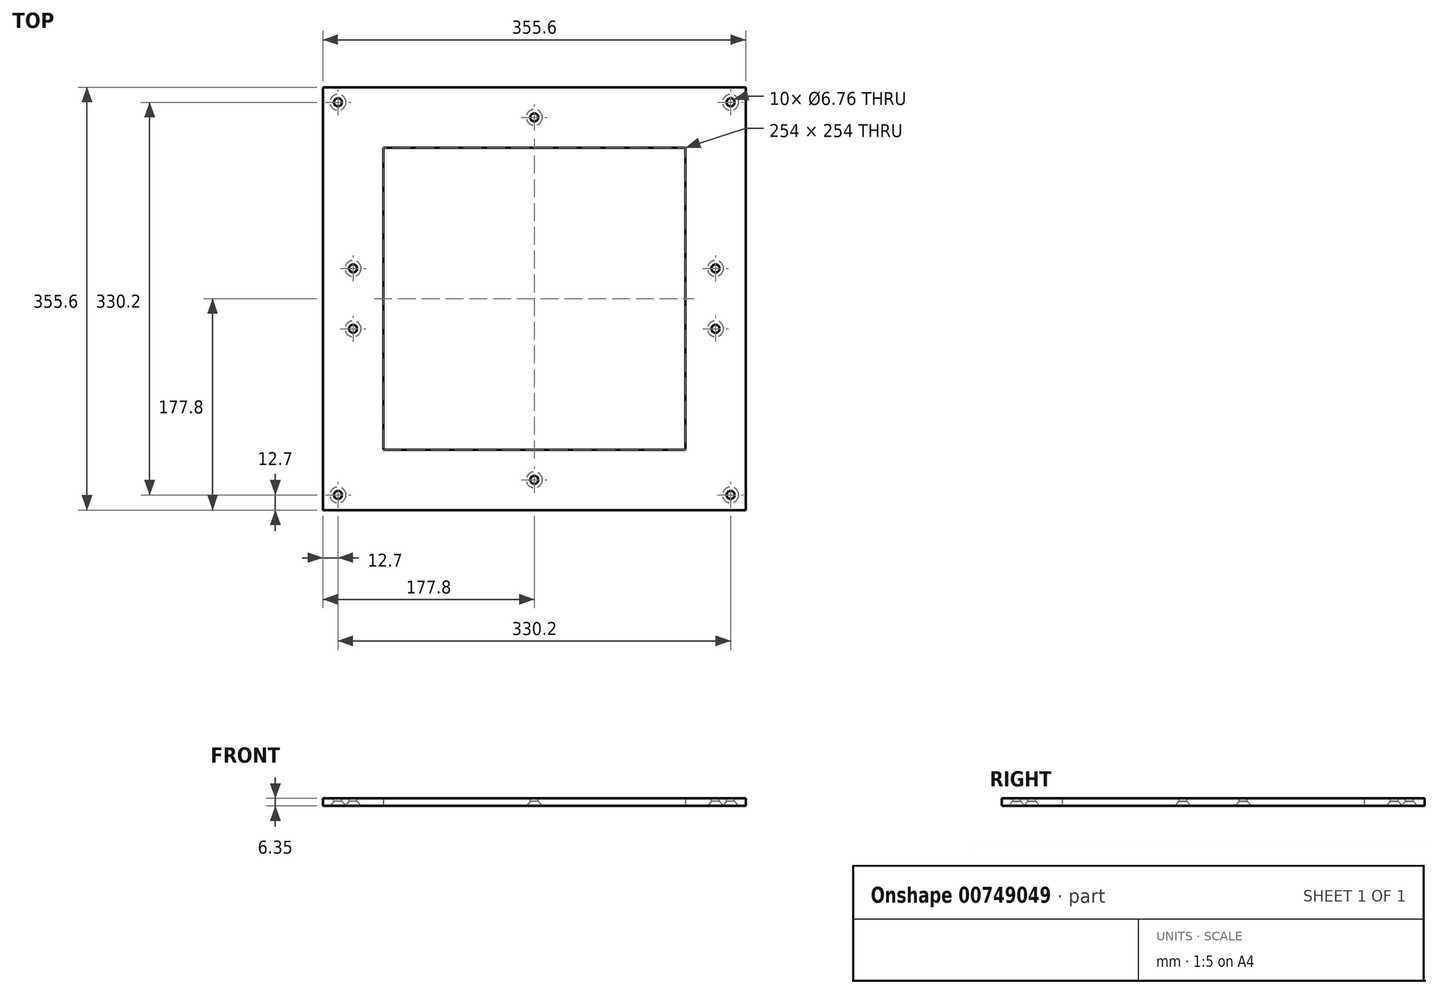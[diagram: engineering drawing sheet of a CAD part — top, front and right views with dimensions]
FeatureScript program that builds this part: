
annotation { "Feature Type Name" : "Feature", "Feature Type Description" : "" }
export const myFeature = defineFeature(function(context is Context, id is Id, definition is map)
    precondition{}
    {
        {
            var Q0;
            Q0=qCreatedBy(makeId("Top.planeOp"),FACE);
            var sketch = newSketch(context, id + "F0", { "sketchPlane" : qUnion([Q0])});
            skLineSegment(sketch, "E0.bottom", {"start": v(0, 0) * mm, "end": v(355.6, 0) * mm});
            skLineSegment(sketch, "E0.top", {"start": v(0, 355.6) * mm, "end": v(355.6, 355.6) * mm});
            skLineSegment(sketch, "E0.left", {"start": v(0, 0) * mm, "end": v(0, 355.6) * mm});
            skLineSegment(sketch, "E0.right", {"start": v(355.6, 0) * mm, "end": v(355.6, 355.6) * mm});
            skLineSegment(sketch, "E1.bottom", {"start": v(304.8, 50.8) * mm, "end": v(50.8, 50.8) * mm});
            skLineSegment(sketch, "E1.top", {"start": v(304.8, 304.8) * mm, "end": v(50.8, 304.8) * mm});
            skLineSegment(sketch, "E1.left", {"start": v(304.8, 50.8) * mm, "end": v(304.8, 304.8) * mm});
            skLineSegment(sketch, "E1.right", {"start": v(50.8, 50.8) * mm, "end": v(50.8, 304.8) * mm});
            skPoint(sketch, "E1.middle", {"position": v(177.8, 177.8) * mm});
            skPoint(sketch, "E1.middle.positionSnap0", {"position": v(177.8, 355.6) * mm});
            skPoint(sketch, "E1.middle.positionSnap1", {"position": v(0, 177.8) * mm});
            skPoint(sketch, "E1.centerSnap0", {"position": v(177.8, 355.6) * mm});
            skPoint(sketch, "E1.centerSnap1", {"position": v(0, 177.8) * mm});
            skLineSegment(sketch, "E2", {"start": v(177.8, 355.6) * mm, "end": v(177.8, 0) * mm, "construction": true});
            skLineSegment(sketch, "E3", {"start": v(0, 177.8) * mm, "end": v(355.6, 177.8) * mm, "construction": true});
            skPoint(sketch, "E4", {"position": v(12.7, 342.9) * mm});
            skPoint(sketch, "E5.MirrorP", {"position": v(342.9, 342.9) * mm});
            skPoint(sketch, "E6.MirrorP", {"position": v(342.9, 12.7) * mm});
            skPoint(sketch, "E7.MirrorP", {"position": v(12.7, 12.7) * mm});
            skPoint(sketch, "E8", {"position": v(177.8, 330.2) * mm});
            skPoint(sketch, "E9.MirrorP", {"position": v(177.8, 25.4) * mm});
            skPoint(sketch, "E10", {"position": v(25.4, 203.2) * mm});
            skPoint(sketch, "E11.MirrorP", {"position": v(25.4, 152.4) * mm});
            skPoint(sketch, "E12.MirrorP", {"position": v(330.2, 203.2) * mm});
            skPoint(sketch, "E13.MirrorP", {"position": v(330.2, 152.4) * mm});
            skSolve(sketch);
        }
        {
            var Q0;
            Q0 = qSketchRegion(id + "F0", true);
            extrude(context, id + "F1", {"entities" : qUnion([Q0]), "depth" : 6.35 * mm, "offsetDistance" : 25.4 * mm});
        }
        {
            var Q0;
            Q0=sQuery(id+"F0.wireOp",VERTEX,"E4");
            var Q1;
            Q1=sQuery(id+"F0.wireOp",VERTEX,"E5.MirrorP");
            var Q2;
            Q2=sQuery(id+"F0.wireOp",VERTEX,"E6.MirrorP");
            var Q3;
            Q3=sQuery(id+"F0.wireOp",VERTEX,"E7.MirrorP");
            var Q4;
            Q4=sQuery(id+"F0.wireOp",VERTEX,"ad2e75b9-914a-43e5-bd15-31be4ab1a6dc");
            var Q5;
            Q5=sQuery(id+"F0.wireOp",VERTEX,"8d2f6cd5-2246-4319-ae9f-100e7987d6fa0.MirrorP");
            var Q6;
            Q6=sQuery(id+"F0.wireOp",VERTEX,"E9.MirrorP");
            var Q7;
            Q7=sQuery(id+"F0.wireOp",VERTEX,"6e66a6cc-68d0-4793-837f-b2f6b6c51e2d0.MirrorP");
            var Q8;
            Q8=sQuery(id+"F0.wireOp",VERTEX,"6aaa8792-5c7a-4e4a-bd7e-9881cde7035a0.MirrorP");
            var Q9;
            Q9=sQuery(id+"F0.wireOp",VERTEX,"E8");
            var Q10;
            Q10=sQuery(id+"F0.wireOp",VERTEX,"E11.MirrorP");
            var Q11;
            Q11=sQuery(id+"F0.wireOp",VERTEX,"E12.MirrorP");
            var Q12;
            Q12=sQuery(id+"F0.wireOp",VERTEX,"E13.MirrorP");
            var Q13;
            Q13=sQuery(id+"F0.wireOp",VERTEX,"E10");
            var Q14;
            Q14=makeQuery(id+"F1.opExtrude","SWEPT_BODY",BODY,{"disambiguationData":[OSD([sQuery(id+"F0.wireOp",EDGE,"E0.bottom"),sQuery(id+"F0.wireOp",EDGE,"E0.top"),sQuery(id+"F0.wireOp",EDGE,"E0.left"),sQuery(id+"F0.wireOp",EDGE,"E0.right"),sQuery(id+"F0.wireOp",EDGE,"E1.bottom"),sQuery(id+"F0.wireOp",EDGE,"E1.top"),sQuery(id+"F0.wireOp",EDGE,"E1.left"),sQuery(id+"F0.wireOp",EDGE,"E1.right")])]});
            hole(context, id + "F2", {"style" : HoleStyle.C_SINK, "endStyle" : HoleEndStyle.BLIND, "oppositeDirection" : true, "standardTappedOrClearance" : lookupTablePath({ "standard" : "ANSI", "fit" : "Normal (ASME)", "size" : "1/4", "type" : "Clearance" }), "standardBlindInLast" : lookupTablePath({ "fit" : "Free", "standard" : "ANSI", "size" : "1/4", "type" : "Clearance" }), "holeDiameter" : 6.76 * mm, "cSinkDiameter" : 13.5 * mm, "cSinkAngle" : 82 * degree, "majorDiameter" : 6.35 * mm, "holeDepth" : 26.06 * mm, "isTappedThrough" : true, "tappedDepth" : 22.25 * mm, "tapClearance" : 3, "locations" : qUnion([Q0, Q1, Q2, Q3, Q4, Q5, Q6, Q7, Q8, Q9, Q10, Q11, Q12, Q13]), "scope" : qUnion([Q14])});
        }
    });
